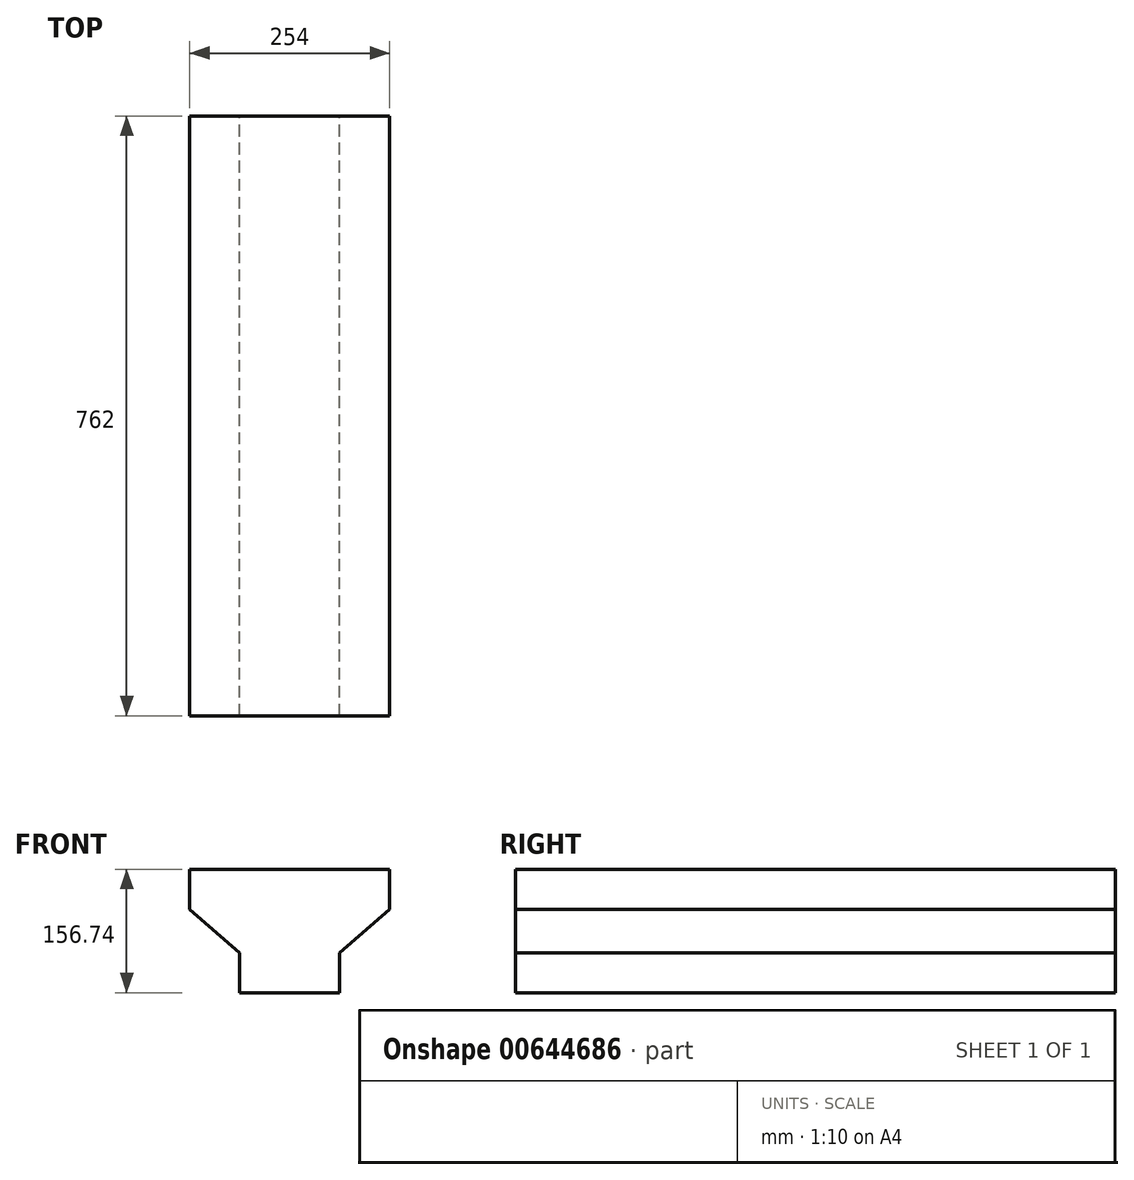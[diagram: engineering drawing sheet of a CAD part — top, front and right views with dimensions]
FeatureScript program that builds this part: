
annotation { "Feature Type Name" : "Feature", "Feature Type Description" : "" }
export const myFeature = defineFeature(function(context is Context, id is Id, definition is map)
    precondition{}
    {
        {
            var Q0;
            Q0=qCreatedBy(makeId("Front.planeOp"),FACE);
            var sketch = newSketch(context, id + "F0", { "sketchPlane" : qUnion([Q0])});
            skLineSegment(sketch, "E0", {"start": v(-121.3, 0) * mm, "end": v(-121.3, 50.8) * mm});
            skLineSegment(sketch, "E1", {"start": v(-121.3, 50.8) * mm, "end": v(132.7, 50.8) * mm});
            skLineSegment(sketch, "E2", {"start": v(132.7, 50.8) * mm, "end": v(132.7, 0) * mm});
            skLineSegment(sketch, "E3", {"start": v(132.7, 0) * mm, "end": v(69.2, -55.14) * mm});
            skLineSegment(sketch, "E4", {"start": v(69.2, -55.14) * mm, "end": v(69.2, -105.94) * mm});
            skLineSegment(sketch, "E5", {"start": v(69.2, -105.94) * mm, "end": v(-57.8, -105.94) * mm});
            skLineSegment(sketch, "E6", {"start": v(-57.8, -105.94) * mm, "end": v(-57.8, -55.14) * mm});
            skLineSegment(sketch, "E7", {"start": v(-57.8, -55.14) * mm, "end": v(-121.3, 0) * mm});
            skSolve(sketch);
        }
        {
            var Q0;
            Q0=makeQuery(id+"F0.imprint","IMPRINT",FACE,{"disambiguationData":[TD([[makeQuery(id+"F0.imprint","IMPRINT",EDGE,{"derivedFrom":sQuery(id+"F0.wireOp",EDGE,"E0")}),-1.0]])]});
            extrude(context, id + "F1", {"entities" : qUnion([Q0]), "depth" : 762 * mm, "offsetDistance" : 25.4 * mm});
        }
    });
